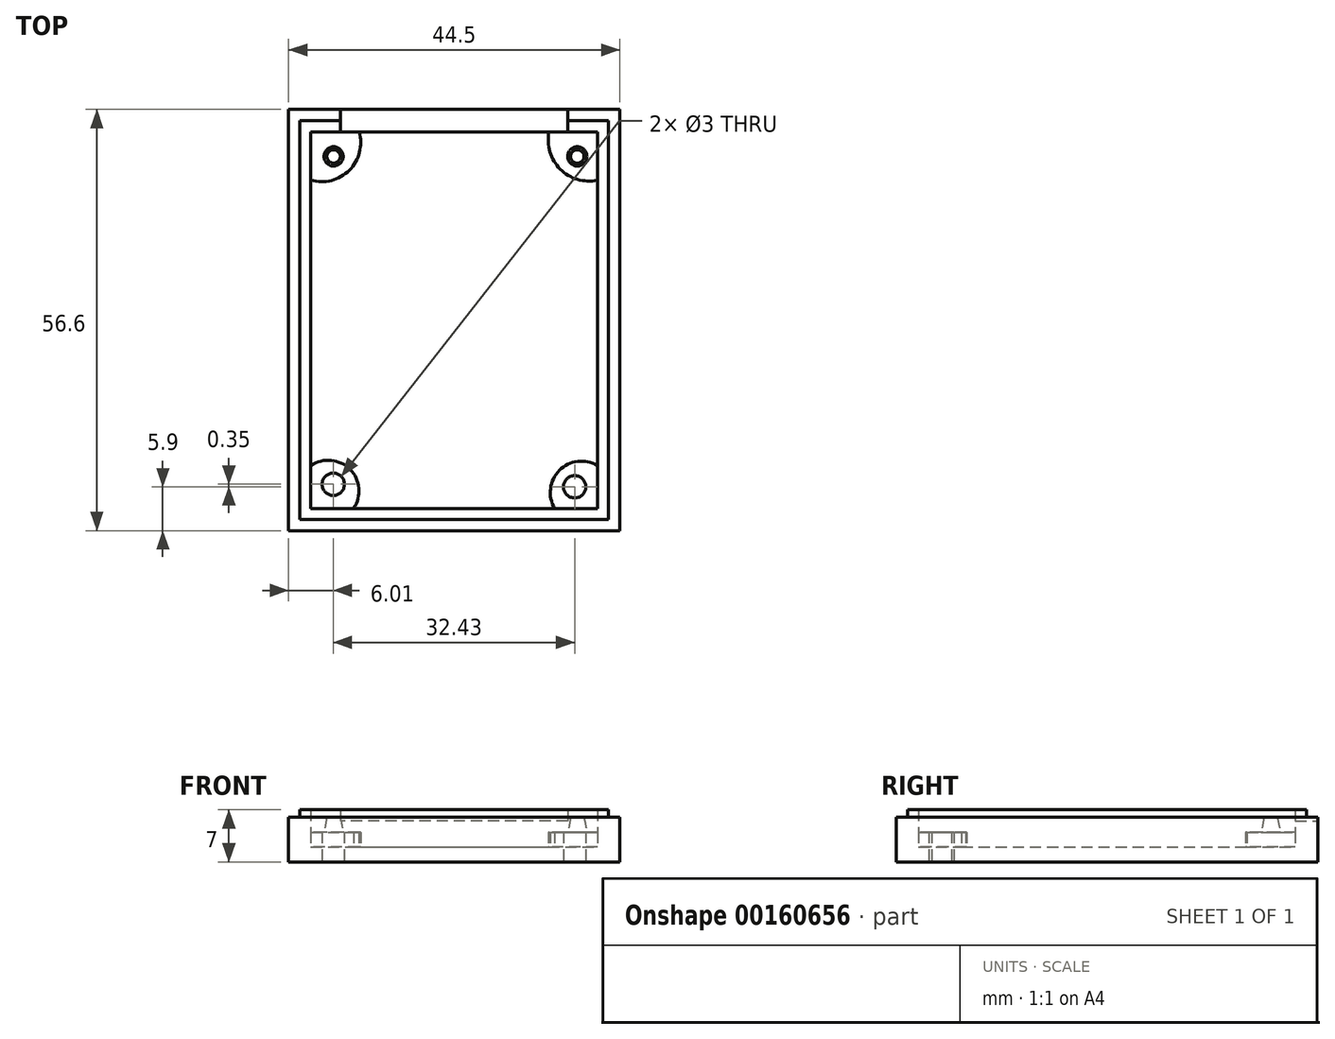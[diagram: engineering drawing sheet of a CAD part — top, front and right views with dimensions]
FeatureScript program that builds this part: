
annotation { "Feature Type Name" : "Feature", "Feature Type Description" : "" }
export const myFeature = defineFeature(function(context is Context, id is Id, definition is map)
    precondition{}
    {
        {
            var Q0;
            Q0=qCreatedBy(makeId("Top.planeOp"),FACE);
            var sketch = newSketch(context, id + "F0", { "sketchPlane" : qUnion([Q0])});
            skLineSegment(sketch, "E0.bottom", {"start": v(0, 0) * mm, "end": v(38.5, 0) * mm});
            skLineSegment(sketch, "E0.top", {"start": v(0, 50.6) * mm, "end": v(38.5, 50.6) * mm});
            skLineSegment(sketch, "E0.left", {"start": v(0, 0) * mm, "end": v(0, 50.6) * mm});
            skLineSegment(sketch, "E0.right", {"start": v(38.5, 0) * mm, "end": v(38.5, 50.6) * mm});
            skCircle(sketch, "E1", {"center": v(3, 3.25) * mm, "radius": 1.5 * mm});
            skCircle(sketch, "E2", {"center": v(35.44, 2.9) * mm, "radius": 1.5 * mm});
            skCircle(sketch, "E3", {"center": v(35.8, 47.3) * mm, "radius": 1.3 * mm});
            skCircle(sketch, "E4", {"center": v(3.05, 47.3) * mm, "radius": 1.3 * mm});
            skArc(sketch, "E5", {"start": v(5.75, 0) * mm, "mid": v(5.26, 5.26) * mm, "end": v(0, 5.75) * mm});
            skArc(sketch, "E6", {"start": v(38.5, 5.75) * mm, "mid": v(33.4, 5.1) * mm, "end": v(32.75, 0) * mm});
            skLineSegment(sketch, "E7.0", {"start": v(-3, -3) * mm, "end": v(-3, 53.6) * mm});
            skLineSegment(sketch, "E7.1", {"start": v(-3, -3) * mm, "end": v(41.5, -3) * mm});
            skLineSegment(sketch, "E7.2", {"start": v(41.5, -3) * mm, "end": v(41.5, 53.6) * mm});
            skLineSegment(sketch, "E7.3", {"start": v(-3, 53.6) * mm, "end": v(41.5, 53.6) * mm});
            skLineSegment(sketch, "E8.0", {"start": v(40, -1.5) * mm, "end": v(40, 52.1) * mm});
            skLineSegment(sketch, "E8.1", {"start": v(-1.5, -1.5) * mm, "end": v(40, -1.5) * mm});
            skLineSegment(sketch, "E8.2", {"start": v(-1.5, -1.5) * mm, "end": v(-1.5, 52.1) * mm});
            skLineSegment(sketch, "E8.3", {"start": v(-1.5, 52.1) * mm, "end": v(40, 52.1) * mm});
            skArc(sketch, "E9", {"start": v(0, 44.1) * mm, "mid": v(5.16, 45.44) * mm, "end": v(6.5, 50.6) * mm});
            skArc(sketch, "E10", {"start": v(32, 50.6) * mm, "mid": v(33.5, 45.6) * mm, "end": v(38.5, 44.1) * mm});
            skSolve(sketch);
        }
        {
            var Q0;
            {var subQ3=sQuery(id+"F0.wireOp",EDGE,"7tGleUKB-KS3F-ii3e-B4WY-jXSfspbsas1K");Q0=makeQuery(id+"F0.imprint","IMPRINT",FACE,{"disambiguationData":[TD([[makeQuery(id+"F0.imprint","IMPRINT",EDGE,{"derivedFrom":subQ3}),-1.0]])]});}
            var Q1;
            {var subQ3=sQuery(id+"F0.wireOp",EDGE,"E5");Q1=makeQuery(id+"F0.imprint","IMPRINT",FACE,{"disambiguationData":[TD([[makeQuery(id+"F0.imprint","IMPRINT",EDGE,{"derivedFrom":subQ3}),-1.0]])]});}
            extrude(context, id + "F1", {"entities" : qUnion([Q0, Q1]), "depth" : 2 * mm});
        }
        {
            var Q0;
            Q0=makeQuery(id+"F0.imprint","IMPRINT",FACE,{"disambiguationData":[TD([[makeQuery(id+"F0.imprint","IMPRINT",EDGE,{"derivedFrom":sQuery(id+"F0.wireOp",EDGE,"E4")}),-1.0]])]});
            var Q1;
            Q1=makeQuery(id+"F0.imprint","IMPRINT",FACE,{"disambiguationData":[TD([[makeQuery(id+"F0.imprint","IMPRINT",EDGE,{"derivedFrom":sQuery(id+"F0.wireOp",EDGE,"E3")}),-1.0]])]});
            var Q2;
            Q2=makeQuery(id+"F0.imprint","IMPRINT",FACE,{"disambiguationData":[TD([[makeQuery(id+"F0.imprint","IMPRINT",EDGE,{"derivedFrom":sQuery(id+"F0.wireOp",EDGE,"E2")}),-1.0]])]});
            var Q3;
            Q3=makeQuery(id+"F0.imprint","IMPRINT",FACE,{"disambiguationData":[TD([[makeQuery(id+"F0.imprint","IMPRINT",EDGE,{"derivedFrom":sQuery(id+"F0.wireOp",EDGE,"E1")}),-1.0]])]});
            extrude(context, id + "F2", {"entities" : qUnion([Q0, Q1, Q2, Q3]), "operationType" : NewBodyOperationType.ADD, "depth" : 4 * mm});
        }
        {
            var Q0;
            Q0=makeQuery(id+"F0.imprint","IMPRINT",FACE,{"disambiguationData":[TD([[makeQuery(id+"F0.imprint","IMPRINT",EDGE,{"derivedFrom":sQuery(id+"F0.wireOp",EDGE,"E4")}),1.0]])]});
            var Q1;
            Q1=makeQuery(id+"F0.imprint","IMPRINT",FACE,{"disambiguationData":[TD([[makeQuery(id+"F0.imprint","IMPRINT",EDGE,{"derivedFrom":sQuery(id+"F0.wireOp",EDGE,"E3")}),1.0]])]});
            extrude(context, id + "F3", {"entities" : qUnion([Q0, Q1]), "operationType" : NewBodyOperationType.ADD, "depth" : 6 * mm});
        }
        {
            var Q0;
            Q0=makeQuery(id+"F0.imprint","IMPRINT",FACE,{"disambiguationData":[TD([[makeQuery(id+"F0.imprint","IMPRINT",EDGE,{"derivedFrom":sQuery(id+"F0.wireOp",EDGE,"E8.0")}),1.0]])]});
            extrude(context, id + "F4", {"entities" : qUnion([Q0]), "operationType" : NewBodyOperationType.ADD, "depth" : 7 * mm});
        }
        {
            var Q0;
            Q0=makeQuery(id+"F0.imprint","IMPRINT",FACE,{"disambiguationData":[TD([[makeQuery(id+"F0.imprint","IMPRINT",EDGE,{"derivedFrom":sQuery(id+"F0.wireOp",EDGE,"E7.0")}),-1.0]])]});
            extrude(context, id + "F5", {"entities" : qUnion([Q0]), "operationType" : NewBodyOperationType.ADD, "depth" : 6 * mm});
        }
        {
            var Q0;
            Q0=makeQuery(id+"F5.opExtrude","SWEPT_FACE",FACE,{"disambiguationData":[OSD([sQuery(id+"F0.wireOp",EDGE,"E7.3")])]});
            var sketch = newSketch(context, id + "F6", { "sketchPlane" : qUnion([Q0])});
            skLineSegment(sketch, "E11.bottom", {"start": v(-34.5, 7) * mm, "end": v(-4, 7) * mm});
            skLineSegment(sketch, "E11.top", {"start": v(-34.5, 5.5) * mm, "end": v(-4, 5.5) * mm});
            skLineSegment(sketch, "E11.left", {"start": v(-34.5, 7) * mm, "end": v(-34.5, 5.5) * mm});
            skLineSegment(sketch, "E11.right", {"start": v(-4, 7) * mm, "end": v(-4, 5.5) * mm});
            skSolve(sketch);
        }
        {
            var Q0;
            Q0 = qSketchRegion(id + "F6", true);
            extrude(context, id + "F7", {"entities" : qUnion([Q0]), "operationType" : NewBodyOperationType.REMOVE, "oppositeDirection" : true, "depth" : 3 * mm});
        }
        {
            var Q0;
            Q0=makeQuery(id+"F3.opExtrude","CAP_EDGE",EDGE,{"disambiguationData":[OSD([sQuery(id+"F0.wireOp",EDGE,"E3")])],"isStart":false});
            var Q1;
            Q1=makeQuery(id+"F3.opExtrude","CAP_EDGE",EDGE,{"disambiguationData":[OSD([sQuery(id+"F0.wireOp",EDGE,"E4")])],"isStart":false});
            chamfer(context, id + "F8", {"entities" : qUnion([Q0, Q1]), "chamferType" : ChamferType.OFFSET_ANGLE, "width" : .4 * mm, "oppositeDirection" : false, "angle" : 79 * degree, "tangentPropagation" : true});
        }
    });
